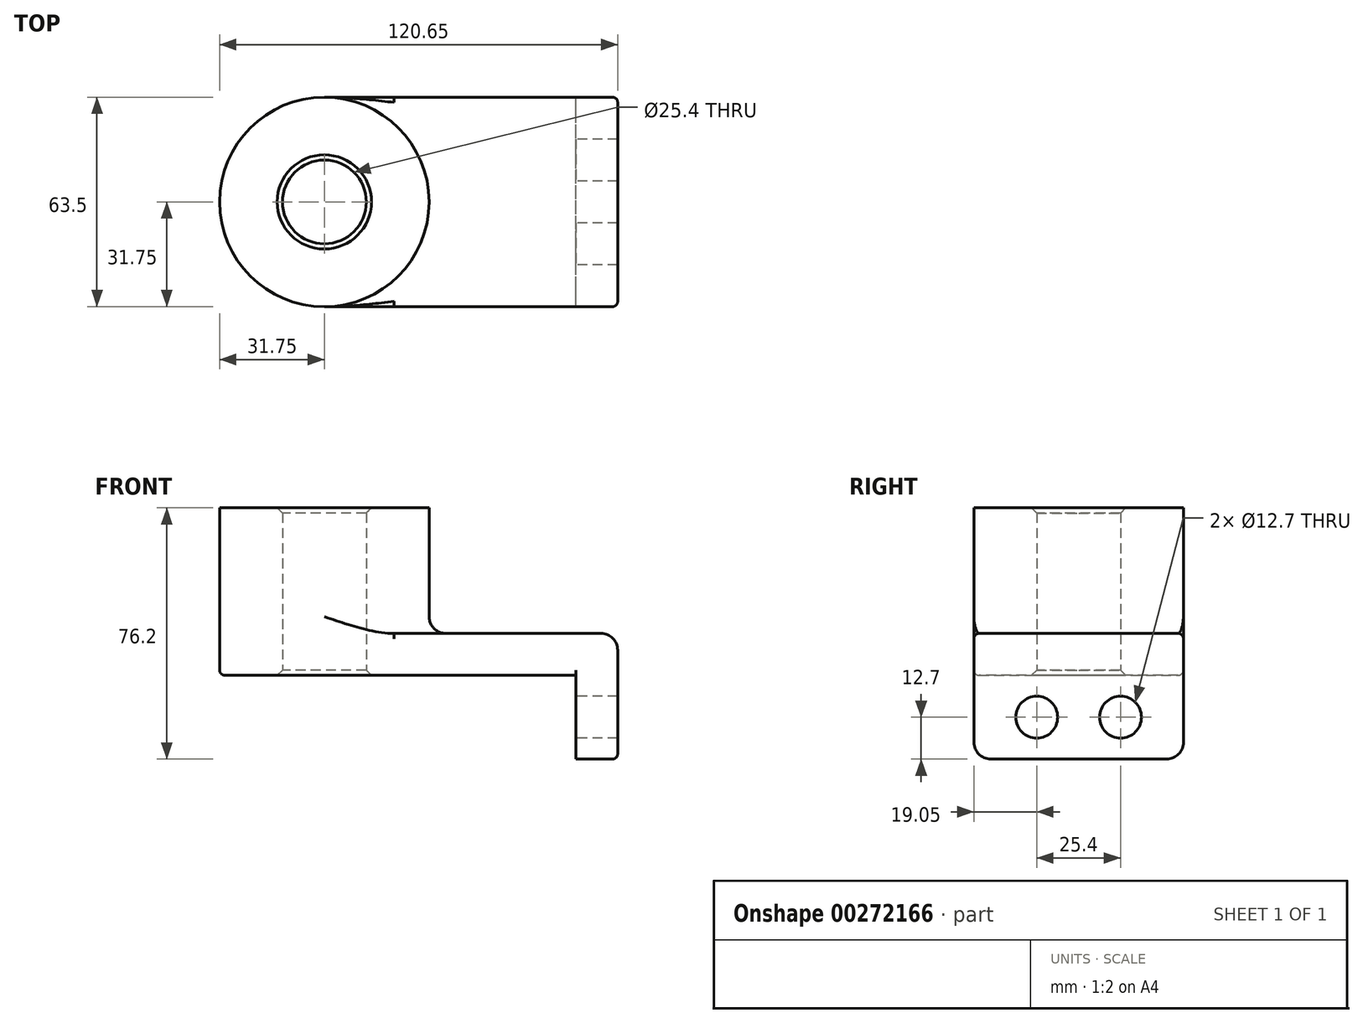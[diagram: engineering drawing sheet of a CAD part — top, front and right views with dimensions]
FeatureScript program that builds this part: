
annotation { "Feature Type Name" : "Feature", "Feature Type Description" : "" }
export const myFeature = defineFeature(function(context is Context, id is Id, definition is map)
    precondition{}
    {
        {
            var Q0;
            Q0=qCreatedBy(makeId("Top.planeOp"),FACE);
            var sketch = newSketch(context, id + "F0", { "sketchPlane" : qUnion([Q0])});
            skLineSegment(sketch, "E0.bottom", {"start": v(38.1, -31.75) * mm, "end": v(-38.1, -31.75) * mm});
            skLineSegment(sketch, "E0.top", {"start": v(38.1, 31.75) * mm, "end": v(-38.1, 31.75) * mm});
            skLineSegment(sketch, "E0.left", {"start": v(38.1, -31.75) * mm, "end": v(38.1, 31.75) * mm});
            skLineSegment(sketch, "E0.right", {"start": v(-38.1, -31.75) * mm, "end": v(-38.1, 31.75) * mm});
            skPoint(sketch, "E0.middle", {"position": v(0, 0) * mm});
            skCircle(sketch, "E1", {"center": v(-38.1, 0) * mm, "radius": 31.75 * mm});
            skCircle(sketch, "E2", {"center": v(-38.1, 0) * mm, "radius": 12.7 * mm});
            skSolve(sketch);
        }
        {
            var Q0;
            Q0 = qSketchRegion(id + "F0", true);
            extrude(context, id + "F1", {"entities" : qUnion([Q0]), "depth" : 12.7 * mm});
        }
        {
            var Q0;
            {var subQ1=sQuery(id+"F0.wireOp",EDGE,"E0.right");var subQ3=sQuery(id+"F0.wireOp",EDGE,"E2");var subQ4=makeQuery(id+"F0.imprint","INTERSECT",VERTEX,{"disambiguationData":[OD(0.0)],"derivedFrom":[subQ1,subQ3]});Q0=makeQuery(id+"F0.imprint","IMPRINT",FACE,{"disambiguationData":[TD([[makeQuery(id+"F0.imprint","IMPRINT",EDGE,{"disambiguationData":[TD([[subQ4,1.0]])],"derivedFrom":subQ3}),-1.0]])]});}
            var Q1;
            {var subQ1=sQuery(id+"F0.wireOp",EDGE,"E0.right");var subQ3=sQuery(id+"F0.wireOp",EDGE,"E2");var subQ4=makeQuery(id+"F0.imprint","INTERSECT",VERTEX,{"disambiguationData":[OD(0.0)],"derivedFrom":[subQ1,subQ3]});Q1=makeQuery(id+"F0.imprint","IMPRINT",FACE,{"disambiguationData":[TD([[makeQuery(id+"F0.imprint","IMPRINT",EDGE,{"disambiguationData":[TD([[subQ4,-1.0]])],"derivedFrom":subQ3}),-1.0]])]});}
            extrude(context, id + "F2", {"entities" : qUnion([Q0, Q1]), "operationType" : NewBodyOperationType.ADD, "depth" : 50.8 * mm});
        }
        {
            var Q0;
            Q0=makeQuery(id+"F1.opExtrude","SWEPT_FACE",FACE,{"disambiguationData":[OSD([sQuery(id+"F0.wireOp",EDGE,"E0.left")])]});
            var sketch = newSketch(context, id + "F3", { "sketchPlane" : qUnion([Q0])});
            skLineSegment(sketch, "E3.bottom", {"start": v(-31.75, 12.7) * mm, "end": v(31.75, 12.7) * mm});
            skLineSegment(sketch, "E3.top", {"start": v(-31.75, -25.4) * mm, "end": v(31.75, -25.4) * mm});
            skLineSegment(sketch, "E3.left", {"start": v(-31.75, 12.7) * mm, "end": v(-31.75, -25.4) * mm});
            skLineSegment(sketch, "E3.right", {"start": v(31.75, 12.7) * mm, "end": v(31.75, -25.4) * mm});
            skCircle(sketch, "E4", {"center": v(-12.7, -12.7) * mm, "radius": 6.35 * mm});
            skLineSegment(sketch, "E5", {"start": v(0, 0) * mm, "end": v(0, -25.4) * mm, "construction": true});
            skCircle(sketch, "E6.MirrorC", {"center": v(12.7, -12.7) * mm, "radius": 6.35 * mm});
            skSolve(sketch);
        }
        {
            var Q0;
            Q0 = qSketchRegion(id + "F3", true);
            extrude(context, id + "F4", {"entities" : qUnion([Q0]), "operationType" : NewBodyOperationType.ADD, "depth" : 12.7 * mm});
        }
        {
            var Q0;
            {var subQ0=sQuery(id+"F0.wireOp",EDGE,"E1");Q0=makeQuery(id+"F2.boolean.opBoolean","INTERSECT",EDGE,{"derivedFrom":[makeQuery(id+"F1.opExtrude","CAP_FACE",FACE,{"disambiguationData":[OSD([sQuery(id+"F0.wireOp",EDGE,"E0.bottom"),sQuery(id+"F0.wireOp",EDGE,"E0.top"),sQuery(id+"F0.wireOp",EDGE,"E0.left"),subQ0,sQuery(id+"F0.wireOp",EDGE,"E2")])],"isStart":false}),makeQuery(id+"F2.opExtrude","SWEPT_FACE",FACE,{"disambiguationData":[OSD([subQ0])]})]});}
            var Q1;
            Q1=makeQuery(id+"F4.opExtrude","CAP_EDGE",EDGE,{"disambiguationData":[OSD([sQuery(id+"F3.wireOp",EDGE,"E3.bottom")])],"isStart":false});
            var Q2;
            Q2=makeQuery(id+"F4.opExtrude","SWEPT_EDGE",EDGE,{"disambiguationData":[OSD([sQuery(id+"F3.wireOp",EDGE,"E3.top"),sQuery(id+"F3.wireOp",EDGE,"E3.right")])]});
            var Q3;
            Q3=makeQuery(id+"F4.opExtrude","SWEPT_EDGE",EDGE,{"disambiguationData":[OSD([sQuery(id+"F3.wireOp",EDGE,"E3.top"),sQuery(id+"F3.wireOp",EDGE,"E3.left")])]});
            fillet(context, id + "F5", {"entities" : qUnion([Q0, Q1, Q2, Q3]), "radius" : 5.08 * mm, "tangentPropagation" : true, "allowEdgeOverflow" : false});
        }
        {
            var Q0;
            Q0=makeQuery(id+"F4.boolean.opBoolean","MERGE",EDGE,{"derivedFrom":[makeQuery(id+"F1.opExtrude","CAP_EDGE",EDGE,{"disambiguationData":[OSD([sQuery(id+"F0.wireOp",EDGE,"E0.bottom")])],"isStart":false}),makeQuery(id+"F4.opExtrude","SWEPT_EDGE",EDGE,{"disambiguationData":[OSD([sQuery(id+"F3.wireOp",EDGE,"E3.bottom"),sQuery(id+"F3.wireOp",EDGE,"E3.left")])]})]});
            var Q1;
            Q1=makeQuery(id+"F1.opExtrude","CAP_EDGE",EDGE,{"disambiguationData":[OSD([sQuery(id+"F0.wireOp",EDGE,"E0.bottom")])],"isStart":true});
            var Q2;
            Q2=makeQuery(id+"F1.opExtrude","CAP_EDGE",EDGE,{"disambiguationData":[OSD([sQuery(id+"F0.wireOp",EDGE,"E0.left")])],"isStart":true});
            fillet(context, id + "F6", {"entities" : qUnion([Q0, Q1, Q2]), "radius" : 1.59 * mm, "tangentPropagation" : true, "allowEdgeOverflow" : false});
        }
        {
            var Q0;
            {var subQ0=sQuery(id+"F0.wireOp",EDGE,"E2");Q0=makeQuery(id+"F2.boolean.opBoolean","MERGE",FACE,{"derivedFrom":[makeQuery(id+"F1.opExtrude","SWEPT_FACE",FACE,{"disambiguationData":[OSD([subQ0])]}),makeQuery(id+"F2.opExtrude","SWEPT_FACE",FACE,{"disambiguationData":[OSD([subQ0])]})]});}
            chamfer(context, id + "F7", {"entities" : qUnion([Q0]), "width" : 1.59 * mm, "tangentPropagation" : true});
        }
    });
